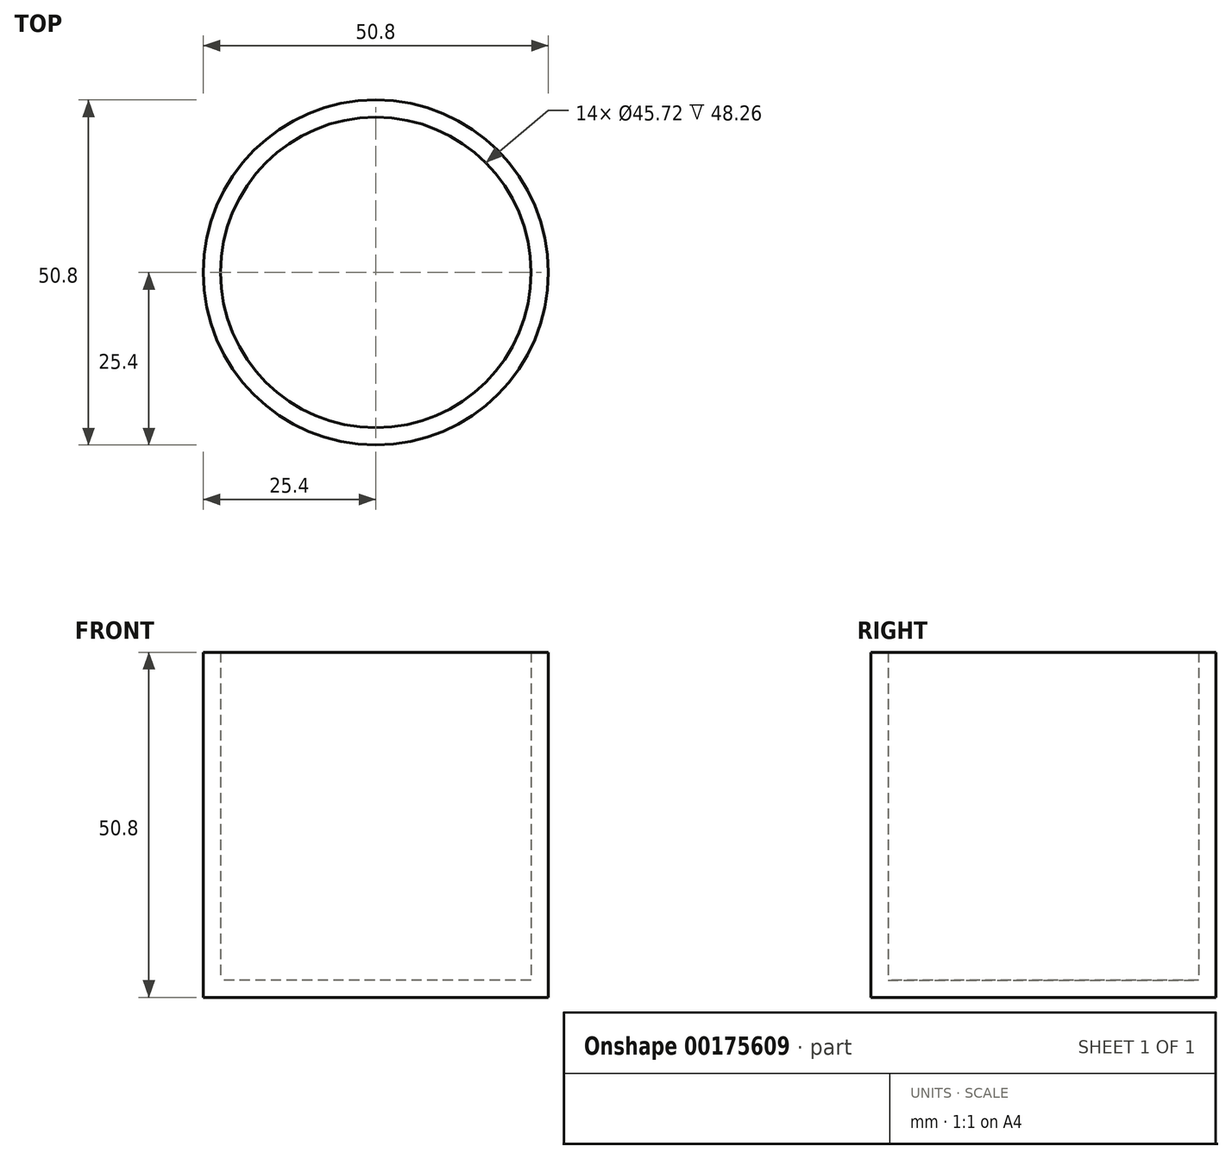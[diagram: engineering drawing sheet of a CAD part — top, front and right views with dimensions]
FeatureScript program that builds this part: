
annotation { "Feature Type Name" : "Feature", "Feature Type Description" : "" }
export const myFeature = defineFeature(function(context is Context, id is Id, definition is map)
    precondition{}
    {
        {
            var Q0;
            Q0=qCreatedBy(makeId("Top.planeOp"),FACE);
            var sketch = newSketch(context, id + "F0", { "sketchPlane" : qUnion([Q0])});
            skCircle(sketch, "E0", {"center": v(0, 0) * mm, "radius": 25.4 * mm});
            skSolve(sketch);
        }
        {
            var Q0;
            Q0=makeQuery(id+"F0.imprint","IMPRINT",FACE,{"disambiguationData":[TD([[makeQuery(id+"F0.imprint","IMPRINT",EDGE,{"derivedFrom":sQuery(id+"F0.wireOp",EDGE,"E0")}),1.0]])]});
            extrude(context, id + "F1", {"entities" : qUnion([Q0]), "depth" : 50.8 * mm});
        }
        {
            var Q0;
            Q0=makeQuery(id+"F1.opExtrude","CAP_FACE",FACE,{"disambiguationData":[OSD([sQuery(id+"F0.wireOp",EDGE,"E0")])],"isStart":false});
            var Q1;
            Q1=makeQuery(id+"F1.opExtrude","SWEPT_BODY",BODY,{"disambiguationData":[OSD([sQuery(id+"F0.wireOp",EDGE,"E0")])]});
            shell(context, id + "F2", {"entities" : qUnion([Q0]), "parts" : qUnion([Q1]), "thickness" : 2.54 * mm});
        }
    });
